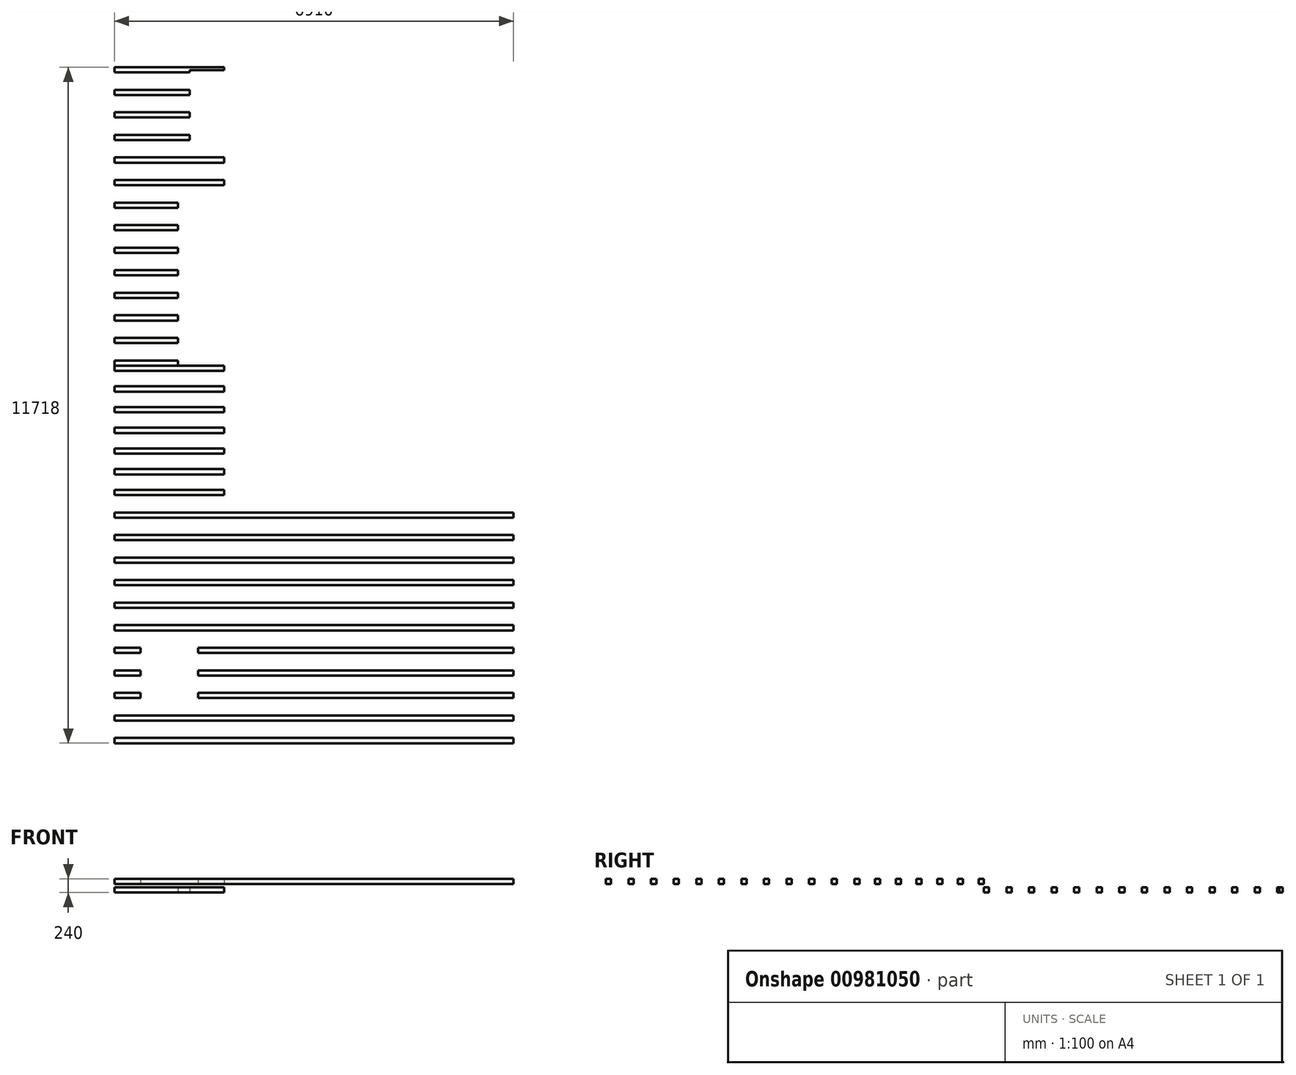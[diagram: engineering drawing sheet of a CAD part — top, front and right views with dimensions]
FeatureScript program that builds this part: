
annotation { "Feature Type Name" : "Feature", "Feature Type Description" : "" }
export const myFeature = defineFeature(function(context is Context, id is Id, definition is map)
    precondition{}
    {
        {
            var Q0;
            Q0=qCreatedBy(makeId("Top.planeOp"),FACE);
            var sketch = newSketch(context, id + "F0", { "sketchPlane" : qUnion([Q0])});
            skLineSegment(sketch, "E0.bottom", {"start": v(-1816.35, -103.72) * mm, "end": v(5093.65, -103.72) * mm});
            skLineSegment(sketch, "E0.top", {"start": v(-1816.35, -13.72) * mm, "end": v(5093.65, -13.72) * mm});
            skLineSegment(sketch, "E0.left", {"start": v(-1816.35, -103.72) * mm, "end": v(-1816.35, -13.72) * mm});
            skLineSegment(sketch, "E0.right", {"start": v(5093.65, -103.72) * mm, "end": v(5093.65, -13.72) * mm});
            skLineSegment(sketch, "E1.0.1.0", {"start": v(-1816.35, 287.28) * mm, "end": v(5093.65, 287.28) * mm});
            skLineSegment(sketch, "E1.0.1.1", {"start": v(-1816.35, 377.28) * mm, "end": v(5093.65, 377.28) * mm});
            skLineSegment(sketch, "E1.0.1.2", {"start": v(5093.65, 287.28) * mm, "end": v(5093.65, 377.28) * mm});
            skLineSegment(sketch, "E1.0.1.3", {"start": v(-1816.35, 287.28) * mm, "end": v(-1816.35, 377.28) * mm});
            skLineSegment(sketch, "E1.direction1", {"start": v(-1816.35, -103.72) * mm, "end": v(-1791.35, -103.72) * mm, "construction": true});
            skLineSegment(sketch, "E1.direction2", {"start": v(-1816.35, -103.72) * mm, "end": v(-1816.35, 287.28) * mm, "construction": true});
            skLineSegment(sketch, "E2.0.0.2", {"start": v(-1816.35, 678.28) * mm, "end": v(5093.65, 678.28) * mm});
            skLineSegment(sketch, "E2.3.0.2", {"start": v(-1816.35, 768.28) * mm, "end": v(5093.65, 768.28) * mm});
            skLineSegment(sketch, "E2.6.0.2", {"start": v(5093.65, 678.28) * mm, "end": v(5093.65, 768.28) * mm});
            skLineSegment(sketch, "E2.9.0.2", {"start": v(-1816.35, 678.28) * mm, "end": v(-1816.35, 768.28) * mm});
            skLineSegment(sketch, "E2.0.0.3", {"start": v(-1816.35, 1069.28) * mm, "end": v(5093.65, 1069.28) * mm});
            skLineSegment(sketch, "E2.3.0.3", {"start": v(-1816.35, 1159.28) * mm, "end": v(5093.65, 1159.28) * mm});
            skLineSegment(sketch, "E2.6.0.3", {"start": v(5093.65, 1069.28) * mm, "end": v(5093.65, 1159.28) * mm});
            skLineSegment(sketch, "E2.9.0.3", {"start": v(-1816.35, 1069.28) * mm, "end": v(-1816.35, 1159.28) * mm});
            skLineSegment(sketch, "E2.0.0.4", {"start": v(-1816.35, 1460.28) * mm, "end": v(5093.65, 1460.28) * mm});
            skLineSegment(sketch, "E2.3.0.4", {"start": v(-1816.35, 1550.28) * mm, "end": v(5093.65, 1550.28) * mm});
            skLineSegment(sketch, "E2.6.0.4", {"start": v(5093.65, 1460.28) * mm, "end": v(5093.65, 1550.28) * mm});
            skLineSegment(sketch, "E2.9.0.4", {"start": v(-1816.35, 1460.28) * mm, "end": v(-1816.35, 1550.28) * mm});
            skLineSegment(sketch, "E2.0.0.5", {"start": v(-1816.35, 1851.28) * mm, "end": v(5093.65, 1851.28) * mm});
            skLineSegment(sketch, "E2.3.0.5", {"start": v(-1816.35, 1941.28) * mm, "end": v(5093.65, 1941.28) * mm});
            skLineSegment(sketch, "E2.6.0.5", {"start": v(5093.65, 1851.28) * mm, "end": v(5093.65, 1941.28) * mm});
            skLineSegment(sketch, "E2.9.0.5", {"start": v(-1816.35, 1851.28) * mm, "end": v(-1816.35, 1941.28) * mm});
            skLineSegment(sketch, "E2.0.0.6", {"start": v(-1816.35, 2242.28) * mm, "end": v(5093.65, 2242.28) * mm});
            skLineSegment(sketch, "E2.3.0.6", {"start": v(-1816.35, 2332.28) * mm, "end": v(5093.65, 2332.28) * mm});
            skLineSegment(sketch, "E2.6.0.6", {"start": v(5093.65, 2242.28) * mm, "end": v(5093.65, 2332.28) * mm});
            skLineSegment(sketch, "E2.9.0.6", {"start": v(-1816.35, 2242.28) * mm, "end": v(-1816.35, 2332.28) * mm});
            skLineSegment(sketch, "E2.0.0.7", {"start": v(-1816.35, 2633.28) * mm, "end": v(5093.65, 2633.28) * mm});
            skLineSegment(sketch, "E2.3.0.7", {"start": v(-1816.35, 2723.28) * mm, "end": v(5093.65, 2723.28) * mm});
            skLineSegment(sketch, "E2.6.0.7", {"start": v(5093.65, 2633.28) * mm, "end": v(5093.65, 2723.28) * mm});
            skLineSegment(sketch, "E2.9.0.7", {"start": v(-1816.35, 2633.28) * mm, "end": v(-1816.35, 2723.28) * mm});
            skLineSegment(sketch, "E2.0.0.8", {"start": v(-1816.35, 3024.28) * mm, "end": v(5093.65, 3024.28) * mm});
            skLineSegment(sketch, "E2.3.0.8", {"start": v(-1816.35, 3114.28) * mm, "end": v(5093.65, 3114.28) * mm});
            skLineSegment(sketch, "E2.6.0.8", {"start": v(5093.65, 3024.28) * mm, "end": v(5093.65, 3114.28) * mm});
            skLineSegment(sketch, "E2.9.0.8", {"start": v(-1816.35, 3024.28) * mm, "end": v(-1816.35, 3114.28) * mm});
            skLineSegment(sketch, "E2.0.0.9", {"start": v(-1816.35, 3415.28) * mm, "end": v(5093.65, 3415.28) * mm});
            skLineSegment(sketch, "E2.3.0.9", {"start": v(-1816.35, 3505.28) * mm, "end": v(5093.65, 3505.28) * mm});
            skLineSegment(sketch, "E2.6.0.9", {"start": v(5093.65, 3415.28) * mm, "end": v(5093.65, 3505.28) * mm});
            skLineSegment(sketch, "E2.9.0.9", {"start": v(-1816.35, 3415.28) * mm, "end": v(-1816.35, 3505.28) * mm});
            skLineSegment(sketch, "E2.0.0.10", {"start": v(-1816.35, 3806.28) * mm, "end": v(5093.65, 3806.28) * mm});
            skLineSegment(sketch, "E2.3.0.10", {"start": v(-1816.35, 3896.28) * mm, "end": v(5093.65, 3896.28) * mm});
            skLineSegment(sketch, "E2.6.0.10", {"start": v(5093.65, 3806.28) * mm, "end": v(5093.65, 3896.28) * mm});
            skLineSegment(sketch, "E2.9.0.10", {"start": v(-1816.35, 3806.28) * mm, "end": v(-1816.35, 3896.28) * mm});
            skLineSegment(sketch, "E3.bottom", {"start": v(-1816.35, 4197.28) * mm, "end": v(83.65, 4197.28) * mm});
            skLineSegment(sketch, "E3.top", {"start": v(-1816.35, 4287.28) * mm, "end": v(83.65, 4287.28) * mm});
            skLineSegment(sketch, "E3.left", {"start": v(-1816.35, 4197.28) * mm, "end": v(-1816.35, 4287.28) * mm});
            skLineSegment(sketch, "E3.right", {"start": v(83.65, 4197.28) * mm, "end": v(83.65, 4287.28) * mm});
            skLineSegment(sketch, "E4.0.1.0", {"start": v(-1816.35, 4646.28) * mm, "end": v(83.65, 4646.28) * mm});
            skLineSegment(sketch, "E4.0.1.1", {"start": v(-1816.35, 4556.28) * mm, "end": v(-1816.35, 4646.28) * mm});
            skLineSegment(sketch, "E4.0.1.2", {"start": v(-1816.35, 4556.28) * mm, "end": v(83.65, 4556.28) * mm});
            skLineSegment(sketch, "E4.0.1.3", {"start": v(83.65, 4556.28) * mm, "end": v(83.65, 4646.28) * mm});
            skLineSegment(sketch, "E4.0.2.0", {"start": v(-1816.35, 5005.28) * mm, "end": v(83.65, 5005.28) * mm});
            skLineSegment(sketch, "E4.0.2.1", {"start": v(-1816.35, 4915.28) * mm, "end": v(-1816.35, 5005.28) * mm});
            skLineSegment(sketch, "E4.0.2.2", {"start": v(-1816.35, 4915.28) * mm, "end": v(83.65, 4915.28) * mm});
            skLineSegment(sketch, "E4.0.2.3", {"start": v(83.65, 4915.28) * mm, "end": v(83.65, 5005.28) * mm});
            skLineSegment(sketch, "E4.0.3.0", {"start": v(-1816.35, 5364.28) * mm, "end": v(83.65, 5364.28) * mm});
            skLineSegment(sketch, "E4.0.3.1", {"start": v(-1816.35, 5274.28) * mm, "end": v(-1816.35, 5364.28) * mm});
            skLineSegment(sketch, "E4.0.3.2", {"start": v(-1816.35, 5274.28) * mm, "end": v(83.65, 5274.28) * mm});
            skLineSegment(sketch, "E4.0.3.3", {"start": v(83.65, 5274.28) * mm, "end": v(83.65, 5364.28) * mm});
            skLineSegment(sketch, "E4.0.4.0", {"start": v(-1816.35, 5723.28) * mm, "end": v(83.65, 5723.28) * mm});
            skLineSegment(sketch, "E4.0.4.1", {"start": v(-1816.35, 5633.28) * mm, "end": v(-1816.35, 5723.28) * mm});
            skLineSegment(sketch, "E4.0.4.2", {"start": v(-1816.35, 5633.28) * mm, "end": v(83.65, 5633.28) * mm});
            skLineSegment(sketch, "E4.0.4.3", {"start": v(83.65, 5633.28) * mm, "end": v(83.65, 5723.28) * mm});
            skLineSegment(sketch, "E4.0.5.0", {"start": v(-1816.35, 6082.28) * mm, "end": v(83.65, 6082.28) * mm});
            skLineSegment(sketch, "E4.0.5.1", {"start": v(-1816.35, 5992.28) * mm, "end": v(-1816.35, 6082.28) * mm});
            skLineSegment(sketch, "E4.0.5.2", {"start": v(-1816.35, 5992.28) * mm, "end": v(83.65, 5992.28) * mm});
            skLineSegment(sketch, "E4.0.5.3", {"start": v(83.65, 5992.28) * mm, "end": v(83.65, 6082.28) * mm});
            skLineSegment(sketch, "E4.direction1", {"start": v(-1816.35, 4197.28) * mm, "end": v(-1791.35, 4197.28) * mm, "construction": true});
            skLineSegment(sketch, "E4.direction2", {"start": v(-1816.35, 4197.28) * mm, "end": v(-1816.35, 4556.28) * mm, "construction": true});
            skLineSegment(sketch, "E5.0.0.6", {"start": v(-1816.35, 6441.28) * mm, "end": v(83.65, 6441.28) * mm});
            skLineSegment(sketch, "E5.3.0.6", {"start": v(-1816.35, 6351.28) * mm, "end": v(-1816.35, 6441.28) * mm});
            skLineSegment(sketch, "E5.6.0.6", {"start": v(-1816.35, 6351.28) * mm, "end": v(83.65, 6351.28) * mm});
            skLineSegment(sketch, "E5.9.0.6", {"start": v(83.65, 6351.28) * mm, "end": v(83.65, 6441.28) * mm});
            skLineSegment(sketch, "E6.top", {"start": v(-1816.35, 6531.28) * mm, "end": v(83.65, 6531.28) * mm});
            skLineSegment(sketch, "E6.left", {"start": v(-1816.35, 6441.28) * mm, "end": v(-1816.35, 6531.28) * mm});
            skLineSegment(sketch, "E6.right", {"start": v(83.65, 6441.28) * mm, "end": v(83.65, 6531.28) * mm});
            skLineSegment(sketch, "E7.0.1.0", {"start": v(-1816.35, 6922.28) * mm, "end": v(83.65, 6922.28) * mm});
            skLineSegment(sketch, "E7.0.1.1", {"start": v(83.65, 6832.28) * mm, "end": v(83.65, 6922.28) * mm});
            skLineSegment(sketch, "E7.0.1.2", {"start": v(-1816.35, 6832.28) * mm, "end": v(83.65, 6832.28) * mm});
            skLineSegment(sketch, "E7.0.1.3", {"start": v(-1816.35, 6832.28) * mm, "end": v(-1816.35, 6922.28) * mm});
            skLineSegment(sketch, "E7.0.2.0", {"start": v(-1816.35, 7313.28) * mm, "end": v(83.65, 7313.28) * mm});
            skLineSegment(sketch, "E7.0.2.1", {"start": v(83.65, 7223.28) * mm, "end": v(83.65, 7313.28) * mm});
            skLineSegment(sketch, "E7.0.2.2", {"start": v(-1816.35, 7223.28) * mm, "end": v(83.65, 7223.28) * mm});
            skLineSegment(sketch, "E7.0.2.3", {"start": v(-1816.35, 7223.28) * mm, "end": v(-1816.35, 7313.28) * mm});
            skLineSegment(sketch, "E7.0.3.0", {"start": v(-1816.35, 7704.28) * mm, "end": v(83.65, 7704.28) * mm});
            skLineSegment(sketch, "E7.0.3.1", {"start": v(83.65, 7614.28) * mm, "end": v(83.65, 7704.28) * mm});
            skLineSegment(sketch, "E7.0.3.2", {"start": v(-1816.35, 7614.28) * mm, "end": v(83.65, 7614.28) * mm});
            skLineSegment(sketch, "E7.0.3.3", {"start": v(-1816.35, 7614.28) * mm, "end": v(-1816.35, 7704.28) * mm});
            skLineSegment(sketch, "E7.0.4.0", {"start": v(-1816.35, 8095.28) * mm, "end": v(83.65, 8095.28) * mm});
            skLineSegment(sketch, "E7.0.4.1", {"start": v(83.65, 8005.28) * mm, "end": v(83.65, 8095.28) * mm});
            skLineSegment(sketch, "E7.0.4.2", {"start": v(-1816.35, 8005.28) * mm, "end": v(83.65, 8005.28) * mm});
            skLineSegment(sketch, "E7.0.4.3", {"start": v(-1816.35, 8005.28) * mm, "end": v(-1816.35, 8095.28) * mm});
            skLineSegment(sketch, "E7.0.5.0", {"start": v(-1816.35, 8486.28) * mm, "end": v(83.65, 8486.28) * mm});
            skLineSegment(sketch, "E7.0.5.1", {"start": v(83.65, 8396.28) * mm, "end": v(83.65, 8486.28) * mm});
            skLineSegment(sketch, "E7.0.5.2", {"start": v(-1816.35, 8396.28) * mm, "end": v(83.65, 8396.28) * mm});
            skLineSegment(sketch, "E7.0.5.3", {"start": v(-1816.35, 8396.28) * mm, "end": v(-1816.35, 8486.28) * mm});
            skLineSegment(sketch, "E7.0.6.0", {"start": v(-1816.35, 8877.28) * mm, "end": v(83.65, 8877.28) * mm});
            skLineSegment(sketch, "E7.0.6.1", {"start": v(83.65, 8787.28) * mm, "end": v(83.65, 8877.28) * mm});
            skLineSegment(sketch, "E7.0.6.2", {"start": v(-1816.35, 8787.28) * mm, "end": v(83.65, 8787.28) * mm});
            skLineSegment(sketch, "E7.0.6.3", {"start": v(-1816.35, 8787.28) * mm, "end": v(-1816.35, 8877.28) * mm});
            skLineSegment(sketch, "E7.0.7.0", {"start": v(-1816.35, 9268.28) * mm, "end": v(83.65, 9268.28) * mm});
            skLineSegment(sketch, "E7.0.7.1", {"start": v(83.65, 9178.28) * mm, "end": v(83.65, 9268.28) * mm});
            skLineSegment(sketch, "E7.0.7.2", {"start": v(-1816.35, 9178.28) * mm, "end": v(83.65, 9178.28) * mm});
            skLineSegment(sketch, "E7.0.7.3", {"start": v(-1816.35, 9178.28) * mm, "end": v(-1816.35, 9268.28) * mm});
            skLineSegment(sketch, "E7.0.8.0", {"start": v(-1816.35, 9659.28) * mm, "end": v(83.65, 9659.28) * mm});
            skLineSegment(sketch, "E7.0.8.1", {"start": v(83.65, 9569.28) * mm, "end": v(83.65, 9659.28) * mm});
            skLineSegment(sketch, "E7.0.8.2", {"start": v(-1816.35, 9569.28) * mm, "end": v(83.65, 9569.28) * mm});
            skLineSegment(sketch, "E7.0.8.3", {"start": v(-1816.35, 9569.28) * mm, "end": v(-1816.35, 9659.28) * mm});
            skLineSegment(sketch, "E7.0.9.0", {"start": v(-1816.35, 10050.28) * mm, "end": v(83.65, 10050.28) * mm});
            skLineSegment(sketch, "E7.0.9.1", {"start": v(83.65, 9960.28) * mm, "end": v(83.65, 10050.28) * mm});
            skLineSegment(sketch, "E7.0.9.2", {"start": v(-1816.35, 9960.28) * mm, "end": v(83.65, 9960.28) * mm});
            skLineSegment(sketch, "E7.0.9.3", {"start": v(-1816.35, 9960.28) * mm, "end": v(-1816.35, 10050.28) * mm});
            skLineSegment(sketch, "E7.direction1", {"start": v(-1816.35, 6441.28) * mm, "end": v(-1791.35, 6441.28) * mm, "construction": true});
            skLineSegment(sketch, "E7.direction2", {"start": v(-1816.35, 6441.28) * mm, "end": v(-1816.35, 6832.28) * mm, "construction": true});
            skLineSegment(sketch, "E8.0.0.10", {"start": v(-1816.35, 10441.28) * mm, "end": v(83.65, 10441.28) * mm});
            skLineSegment(sketch, "E8.3.0.10", {"start": v(83.65, 10351.28) * mm, "end": v(83.65, 10441.28) * mm});
            skLineSegment(sketch, "E8.6.0.10", {"start": v(-1816.35, 10351.28) * mm, "end": v(83.65, 10351.28) * mm});
            skLineSegment(sketch, "E8.9.0.10", {"start": v(-1816.35, 10351.28) * mm, "end": v(-1816.35, 10441.28) * mm});
            skLineSegment(sketch, "E8.0.0.11", {"start": v(-1816.35, 10832.28) * mm, "end": v(83.65, 10832.28) * mm});
            skLineSegment(sketch, "E8.3.0.11", {"start": v(83.65, 10742.28) * mm, "end": v(83.65, 10832.28) * mm});
            skLineSegment(sketch, "E8.6.0.11", {"start": v(-1816.35, 10742.28) * mm, "end": v(83.65, 10742.28) * mm});
            skLineSegment(sketch, "E8.9.0.11", {"start": v(-1816.35, 10742.28) * mm, "end": v(-1816.35, 10832.28) * mm});
            skLineSegment(sketch, "E8.0.0.12", {"start": v(-1816.35, 11223.28) * mm, "end": v(83.65, 11223.28) * mm});
            skLineSegment(sketch, "E8.3.0.12", {"start": v(83.65, 11133.28) * mm, "end": v(83.65, 11223.28) * mm});
            skLineSegment(sketch, "E8.6.0.12", {"start": v(-1816.35, 11133.28) * mm, "end": v(83.65, 11133.28) * mm});
            skLineSegment(sketch, "E8.9.0.12", {"start": v(-1816.35, 11133.28) * mm, "end": v(-1816.35, 11223.28) * mm});
            skLineSegment(sketch, "E8.0.0.13", {"start": v(-1816.35, 11614.28) * mm, "end": v(83.65, 11614.28) * mm});
            skLineSegment(sketch, "E8.3.0.13", {"start": v(83.65, 11524.28) * mm, "end": v(83.65, 11614.28) * mm});
            skLineSegment(sketch, "E8.6.0.13", {"start": v(-1816.35, 11524.28) * mm, "end": v(83.65, 11524.28) * mm});
            skLineSegment(sketch, "E8.9.0.13", {"start": v(-1816.35, 11524.28) * mm, "end": v(-1816.35, 11614.28) * mm});
            skSolve(sketch);
        }
        {
            var Q0;
            Q0=makeQuery(id+"F0.imprint","IMPRINT",FACE,{"disambiguationData":[TD([[makeQuery(id+"F0.imprint","IMPRINT",EDGE,{"derivedFrom":sQuery(id+"F0.wireOp",EDGE,"E5.3.0.6")}),-1.0]])]});
            var Q1;
            Q1=makeQuery(id+"F0.imprint","IMPRINT",FACE,{"disambiguationData":[TD([[makeQuery(id+"F0.imprint","IMPRINT",EDGE,{"derivedFrom":sQuery(id+"F0.wireOp",EDGE,"E4.0.5.0")}),-1.0]])]});
            var Q2;
            Q2=makeQuery(id+"F0.imprint","IMPRINT",FACE,{"disambiguationData":[TD([[makeQuery(id+"F0.imprint","IMPRINT",EDGE,{"derivedFrom":sQuery(id+"F0.wireOp",EDGE,"E4.0.4.0")}),-1.0]])]});
            var Q3;
            Q3=makeQuery(id+"F0.imprint","IMPRINT",FACE,{"disambiguationData":[TD([[makeQuery(id+"F0.imprint","IMPRINT",EDGE,{"derivedFrom":sQuery(id+"F0.wireOp",EDGE,"E4.0.3.0")}),-1.0]])]});
            var Q4;
            Q4=makeQuery(id+"F0.imprint","IMPRINT",FACE,{"disambiguationData":[TD([[makeQuery(id+"F0.imprint","IMPRINT",EDGE,{"derivedFrom":sQuery(id+"F0.wireOp",EDGE,"E4.0.2.0")}),-1.0]])]});
            var Q5;
            Q5=makeQuery(id+"F0.imprint","IMPRINT",FACE,{"disambiguationData":[TD([[makeQuery(id+"F0.imprint","IMPRINT",EDGE,{"derivedFrom":sQuery(id+"F0.wireOp",EDGE,"E4.0.1.0")}),-1.0]])]});
            var Q6;
            Q6=makeQuery(id+"F0.imprint","IMPRINT",FACE,{"disambiguationData":[TD([[makeQuery(id+"F0.imprint","IMPRINT",EDGE,{"derivedFrom":sQuery(id+"F0.wireOp",EDGE,"E3.bottom")}),1.0]])]});
            var Q7;
            Q7=makeQuery(id+"F0.imprint","IMPRINT",FACE,{"disambiguationData":[TD([[makeQuery(id+"F0.imprint","IMPRINT",EDGE,{"derivedFrom":sQuery(id+"F0.wireOp",EDGE,"E2.0.0.10")}),1.0]])]});
            var Q8;
            Q8=makeQuery(id+"F0.imprint","IMPRINT",FACE,{"disambiguationData":[TD([[makeQuery(id+"F0.imprint","IMPRINT",EDGE,{"derivedFrom":sQuery(id+"F0.wireOp",EDGE,"E2.0.0.9")}),1.0]])]});
            var Q9;
            Q9=makeQuery(id+"F0.imprint","IMPRINT",FACE,{"disambiguationData":[TD([[makeQuery(id+"F0.imprint","IMPRINT",EDGE,{"derivedFrom":sQuery(id+"F0.wireOp",EDGE,"E2.0.0.8")}),1.0]])]});
            var Q10;
            Q10=makeQuery(id+"F0.imprint","IMPRINT",FACE,{"disambiguationData":[TD([[makeQuery(id+"F0.imprint","IMPRINT",EDGE,{"derivedFrom":sQuery(id+"F0.wireOp",EDGE,"E2.0.0.7")}),1.0]])]});
            var Q11;
            Q11=makeQuery(id+"F0.imprint","IMPRINT",FACE,{"disambiguationData":[TD([[makeQuery(id+"F0.imprint","IMPRINT",EDGE,{"derivedFrom":sQuery(id+"F0.wireOp",EDGE,"E2.0.0.6")}),1.0]])]});
            var Q12;
            Q12=makeQuery(id+"F0.imprint","IMPRINT",FACE,{"disambiguationData":[TD([[makeQuery(id+"F0.imprint","IMPRINT",EDGE,{"derivedFrom":sQuery(id+"F0.wireOp",EDGE,"E2.0.0.5")}),1.0]])]});
            var Q13;
            Q13=makeQuery(id+"F0.imprint","IMPRINT",FACE,{"disambiguationData":[TD([[makeQuery(id+"F0.imprint","IMPRINT",EDGE,{"derivedFrom":sQuery(id+"F0.wireOp",EDGE,"E2.0.0.4")}),1.0]])]});
            var Q14;
            Q14=makeQuery(id+"F0.imprint","IMPRINT",FACE,{"disambiguationData":[TD([[makeQuery(id+"F0.imprint","IMPRINT",EDGE,{"derivedFrom":sQuery(id+"F0.wireOp",EDGE,"E2.0.0.3")}),1.0]])]});
            var Q15;
            Q15=makeQuery(id+"F0.imprint","IMPRINT",FACE,{"disambiguationData":[TD([[makeQuery(id+"F0.imprint","IMPRINT",EDGE,{"derivedFrom":sQuery(id+"F0.wireOp",EDGE,"E2.0.0.2")}),1.0]])]});
            var Q16;
            Q16=makeQuery(id+"F0.imprint","IMPRINT",FACE,{"disambiguationData":[TD([[makeQuery(id+"F0.imprint","IMPRINT",EDGE,{"derivedFrom":sQuery(id+"F0.wireOp",EDGE,"E1.0.1.0")}),1.0]])]});
            var Q17;
            Q17=makeQuery(id+"F0.imprint","IMPRINT",FACE,{"disambiguationData":[TD([[makeQuery(id+"F0.imprint","IMPRINT",EDGE,{"derivedFrom":sQuery(id+"F0.wireOp",EDGE,"E0.bottom")}),1.0]])]});
            extrude(context, id + "F1", {"entities" : qUnion([Q0, Q1, Q2, Q3, Q4, Q5, Q6, Q7, Q8, Q9, Q10, Q11, Q12, Q13, Q14, Q15, Q16, Q17]), "depth" : 90 * mm, "offsetDistance" : 25 * mm});
        }
        {
            var Q0;
            Q0=makeQuery(id+"F0.imprint","IMPRINT",FACE,{"disambiguationData":[TD([[makeQuery(id+"F0.imprint","IMPRINT",EDGE,{"derivedFrom":sQuery(id+"F0.wireOp",EDGE,"E5.0.0.6")}),1.0]])]});
            var Q1;
            Q1=makeQuery(id+"F0.imprint","IMPRINT",FACE,{"disambiguationData":[TD([[makeQuery(id+"F0.imprint","IMPRINT",EDGE,{"derivedFrom":sQuery(id+"F0.wireOp",EDGE,"E7.0.1.0")}),-1.0]])]});
            var Q2;
            Q2=makeQuery(id+"F0.imprint","IMPRINT",FACE,{"disambiguationData":[TD([[makeQuery(id+"F0.imprint","IMPRINT",EDGE,{"derivedFrom":sQuery(id+"F0.wireOp",EDGE,"E7.0.2.0")}),-1.0]])]});
            var Q3;
            Q3=makeQuery(id+"F0.imprint","IMPRINT",FACE,{"disambiguationData":[TD([[makeQuery(id+"F0.imprint","IMPRINT",EDGE,{"derivedFrom":sQuery(id+"F0.wireOp",EDGE,"E7.0.3.0")}),-1.0]])]});
            var Q4;
            Q4=makeQuery(id+"F0.imprint","IMPRINT",FACE,{"disambiguationData":[TD([[makeQuery(id+"F0.imprint","IMPRINT",EDGE,{"derivedFrom":sQuery(id+"F0.wireOp",EDGE,"E7.0.4.0")}),-1.0]])]});
            var Q5;
            Q5=makeQuery(id+"F0.imprint","IMPRINT",FACE,{"disambiguationData":[TD([[makeQuery(id+"F0.imprint","IMPRINT",EDGE,{"derivedFrom":sQuery(id+"F0.wireOp",EDGE,"E7.0.5.0")}),-1.0]])]});
            var Q6;
            Q6=makeQuery(id+"F0.imprint","IMPRINT",FACE,{"disambiguationData":[TD([[makeQuery(id+"F0.imprint","IMPRINT",EDGE,{"derivedFrom":sQuery(id+"F0.wireOp",EDGE,"E7.0.6.0")}),-1.0]])]});
            var Q7;
            Q7=makeQuery(id+"F0.imprint","IMPRINT",FACE,{"disambiguationData":[TD([[makeQuery(id+"F0.imprint","IMPRINT",EDGE,{"derivedFrom":sQuery(id+"F0.wireOp",EDGE,"E7.0.7.0")}),-1.0]])]});
            var Q8;
            Q8=makeQuery(id+"F0.imprint","IMPRINT",FACE,{"disambiguationData":[TD([[makeQuery(id+"F0.imprint","IMPRINT",EDGE,{"derivedFrom":sQuery(id+"F0.wireOp",EDGE,"E7.0.8.0")}),-1.0]])]});
            var Q9;
            Q9=makeQuery(id+"F0.imprint","IMPRINT",FACE,{"disambiguationData":[TD([[makeQuery(id+"F0.imprint","IMPRINT",EDGE,{"derivedFrom":sQuery(id+"F0.wireOp",EDGE,"E7.0.9.0")}),-1.0]])]});
            var Q10;
            Q10=makeQuery(id+"F0.imprint","IMPRINT",FACE,{"disambiguationData":[TD([[makeQuery(id+"F0.imprint","IMPRINT",EDGE,{"derivedFrom":sQuery(id+"F0.wireOp",EDGE,"E8.0.0.10")}),-1.0]])]});
            var Q11;
            Q11=makeQuery(id+"F0.imprint","IMPRINT",FACE,{"disambiguationData":[TD([[makeQuery(id+"F0.imprint","IMPRINT",EDGE,{"derivedFrom":sQuery(id+"F0.wireOp",EDGE,"E8.0.0.11")}),-1.0]])]});
            var Q12;
            Q12=makeQuery(id+"F0.imprint","IMPRINT",FACE,{"disambiguationData":[TD([[makeQuery(id+"F0.imprint","IMPRINT",EDGE,{"derivedFrom":sQuery(id+"F0.wireOp",EDGE,"E8.0.0.12")}),-1.0]])]});
            var Q13;
            Q13=makeQuery(id+"F0.imprint","IMPRINT",FACE,{"disambiguationData":[TD([[makeQuery(id+"F0.imprint","IMPRINT",EDGE,{"derivedFrom":sQuery(id+"F0.wireOp",EDGE,"E8.0.0.13")}),-1.0]])]});
            extrude(context, id + "F2", {"entities" : qUnion([Q0, Q1, Q2, Q3, Q4, Q5, Q6, Q7, Q8, Q9, Q10, Q11, Q12, Q13]), "oppositeDirection" : true, "depth" : 150 * mm, "offsetDistance" : 25 * mm, "hasSecondDirection" : true, "secondDirectionOppositeDirection" : true, "secondDirectionDepth" : 60 * mm});
        }
        {
            var Q0;
            Q0=makeQuery(id+"F1.opExtrude","CAP_FACE",FACE,{"disambiguationData":[OSD([sQuery(id+"F0.wireOp",EDGE,"E2.0.0.3"),sQuery(id+"F0.wireOp",EDGE,"E2.3.0.3"),sQuery(id+"F0.wireOp",EDGE,"E2.6.0.3"),sQuery(id+"F0.wireOp",EDGE,"E2.9.0.3")])],"isStart":false});
            var sketch = newSketch(context, id + "F3", { "sketchPlane" : qUnion([Q0])});
            skLineSegment(sketch, "E9.bottom", {"start": v(-1366.35, 396.28) * mm, "end": v(-366.35, 396.28) * mm});
            skLineSegment(sketch, "E9.top", {"start": v(-1366.35, 1846.28) * mm, "end": v(-366.35, 1846.28) * mm});
            skLineSegment(sketch, "E9.left", {"start": v(-1366.35, 396.28) * mm, "end": v(-1366.35, 1846.28) * mm});
            skLineSegment(sketch, "E9.right", {"start": v(-366.35, 396.28) * mm, "end": v(-366.35, 1846.28) * mm});
            skLineSegment(sketch, "E10.bottom", {"start": v(-516.35, 11561.28) * mm, "end": v(83.65, 11561.28) * mm});
            skLineSegment(sketch, "E10.top", {"start": v(-516.35, 10261.28) * mm, "end": v(83.65, 10261.28) * mm});
            skLineSegment(sketch, "E10.left", {"start": v(-516.35, 11561.28) * mm, "end": v(-516.35, 10261.28) * mm});
            skLineSegment(sketch, "E10.right", {"start": v(83.65, 11561.28) * mm, "end": v(83.65, 10261.28) * mm});
            skLineSegment(sketch, "E11.bottom", {"start": v(-716.35, 9552.28) * mm, "end": v(83.65, 9552.28) * mm});
            skLineSegment(sketch, "E11.top", {"start": v(-716.35, 6442.28) * mm, "end": v(83.65, 6442.28) * mm});
            skLineSegment(sketch, "E11.left", {"start": v(-716.35, 9552.28) * mm, "end": v(-716.35, 6442.28) * mm});
            skLineSegment(sketch, "E11.right", {"start": v(83.65, 9552.28) * mm, "end": v(83.65, 6442.28) * mm});
            skSolve(sketch);
        }
        {
            var Q0;
            {var subQ0=sQuery(id+"F3.wireOp",EDGE,"E9.top");Q0=makeQuery(id+"F3.imprint","IMPRINT",FACE,{"disambiguationData":[TD([[makeQuery(id+"F3.imprint","IMPRINT",EDGE,{"derivedFrom":subQ0}),-1.0]])]});}
            var Q1;
            {var subQ0=sQuery(id+"F3.wireOp",EDGE,"E9.bottom");Q1=makeQuery(id+"F3.imprint","IMPRINT",FACE,{"disambiguationData":[TD([[makeQuery(id+"F3.imprint","IMPRINT",EDGE,{"derivedFrom":subQ0}),1.0]])]});}
            var Q2;
            Q2=makeQuery(id+"F3.imprint","IMPRINT",FACE,{"disambiguationData":[TD([[makeQuery(id+"F3.imprint","IMPRINT",EDGE,{"derivedFrom":sQuery(id+"F3.wireOp",EDGE,"E11.bottom")}),-1.0]])]});
            var Q3;
            Q3=makeQuery(id+"F3.imprint","IMPRINT",FACE,{"disambiguationData":[TD([[makeQuery(id+"F3.imprint","IMPRINT",EDGE,{"derivedFrom":sQuery(id+"F3.wireOp",EDGE,"E10.bottom")}),-1.0]])]});
            var Q4;
            {var subQ0=sQuery(id+"F3.wireOp",EDGE,"E9.left");var subQ1=makeQuery(id+"F1.opExtrude","CAP_EDGE",EDGE,{"disambiguationData":[OSD([sQuery(id+"F0.wireOp",EDGE,"E2.0.0.3")])],"isStart":false});var subQ2=makeQuery(id+"F3.imprint","INTERSECT",VERTEX,{"derivedFrom":[subQ1,subQ0]});Q4=makeQuery(id+"F3.imprint","IMPRINT",FACE,{"disambiguationData":[TD([[makeQuery(id+"F3.imprint","IMPRINT",EDGE,{"disambiguationData":[TD([[subQ2,-1.0]])],"derivedFrom":subQ0}),-1.0]])]});}
            extrude(context, id + "F4", {"entities" : qUnion([Q0, Q1, Q2, Q3, Q4]), "operationType" : NewBodyOperationType.REMOVE, "oppositeDirection" : true, "depth" : 1000 * mm, "offsetDistance" : 25 * mm});
        }
    });
